# Revit family: FantiniCosmi_BIM_C16
name_source: partatom
category: Generic Models
units: mm (PartAtom-declared; Revit-internal decimal feet)

## family parameters
Always vertical = Yes
Can host rebar = No
Cut with Voids When Loaded = No
Part Type = Normal
Room Calculation Point = No
Round Connector Dimension = Use Diameter
Shared = No
Work Plane-Based = No

## types (1)
- Standard
    Action type = 1B
    Body admissible temperature = -10 ÷ 50 °C
    Catalog web link = https://www.fantinicosmi.it
    Default Elevation = 0 mm  [stored 0 ft]
    Description = Electromechanical room thermostats with vapor expansion
    Differential = 0,8 K
    Material = Thermoplastic
    Part Number = C16
    Protection degree = IP2
    Temperarure regulation range = 10 ÷ 30 °C
    Weight = 0,14 Kg

note: [stored X ft] marks values corroborated as IEEE doubles in the binary element streams (Revit-internal decimal feet)

## geometry (parser evidence)
native form markers: Sweep x2
no freeform markers — native parametric forms only
